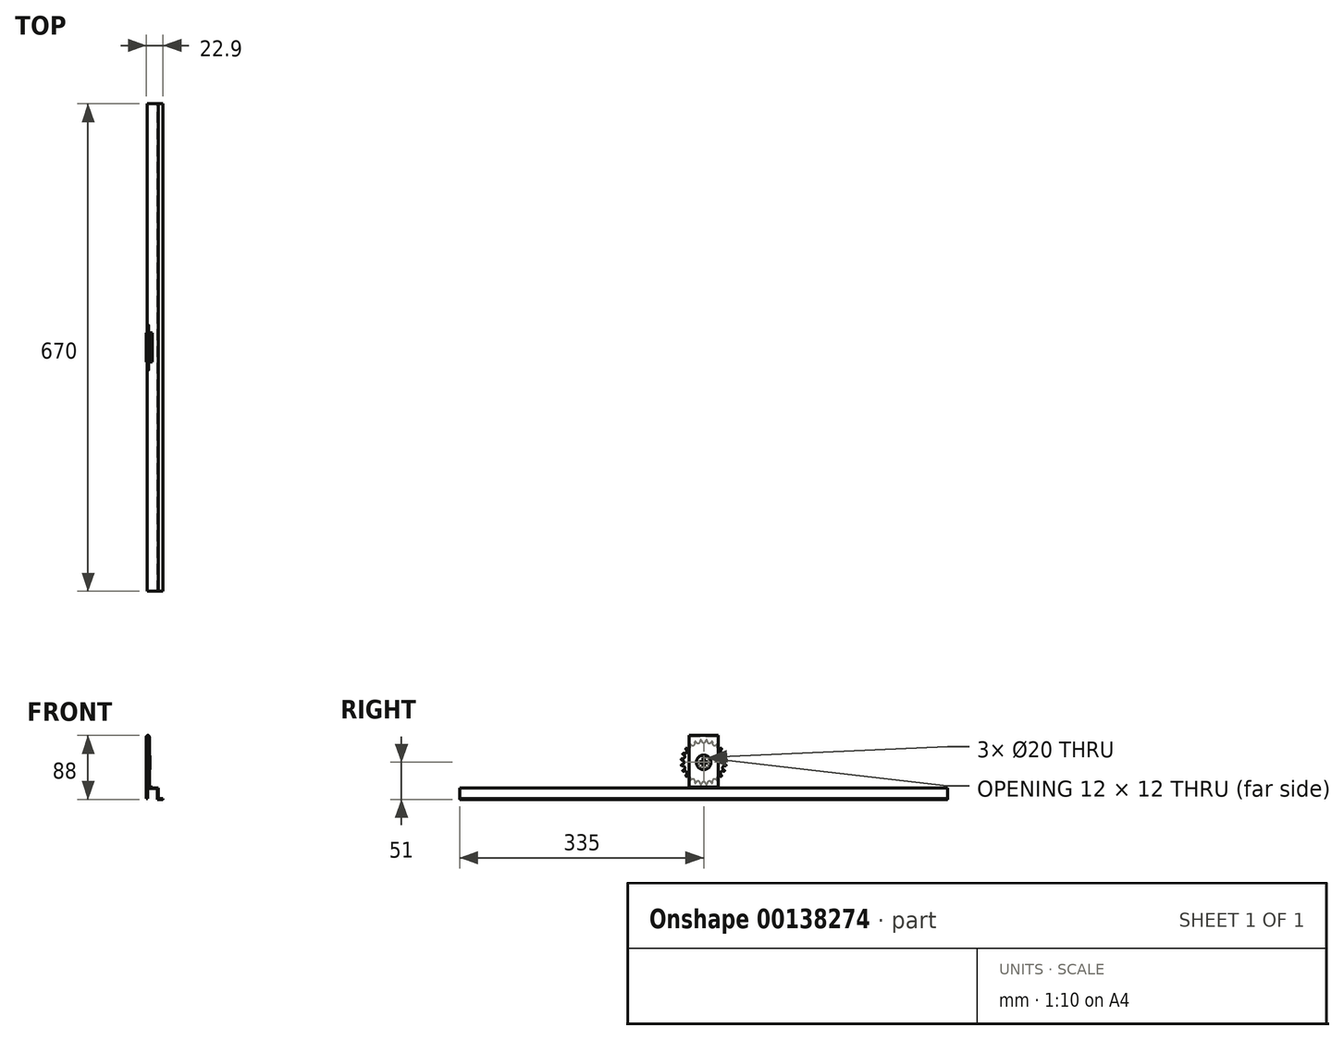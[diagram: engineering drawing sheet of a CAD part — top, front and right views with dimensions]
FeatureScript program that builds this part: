
annotation { "Feature Type Name" : "Feature", "Feature Type Description" : "" }
export const myFeature = defineFeature(function(context is Context, id is Id, definition is map)
    precondition{}
    {
        {
            var Q0;
            Q0=qCreatedBy(makeId("Front.planeOp"),FACE);
            var sketch = newSketch(context, id + "F0", { "sketchPlane" : qUnion([Q0])});
            skLineSegment(sketch, "E0.bottom", {"start": v(0, 0) * mm, "end": v(15, 0) * mm});
            skLineSegment(sketch, "E0.top", {"start": v(1, -1) * mm, "end": v(14, -1) * mm});
            skLineSegment(sketch, "E0.left", {"start": v(0, 0) * mm, "end": v(0, -1) * mm});
            skLineSegment(sketch, "E0.right", {"start": v(15, 0) * mm, "end": v(15, -1) * mm});
            skLineSegment(sketch, "E1.bottom", {"start": v(15, 0) * mm, "end": v(14, 0) * mm});
            skLineSegment(sketch, "E1.top", {"start": v(15, -16) * mm, "end": v(14, -16) * mm});
            skLineSegment(sketch, "E1.left", {"start": v(15, 0) * mm, "end": v(15, -15) * mm});
            skLineSegment(sketch, "E1.right", {"start": v(14, -1) * mm, "end": v(14, -16) * mm});
            skLineSegment(sketch, "E2.bottom", {"start": v(14, -16) * mm, "end": v(21.9, -16) * mm});
            skLineSegment(sketch, "E2.top", {"start": v(15, -15) * mm, "end": v(21.9, -15) * mm});
            skLineSegment(sketch, "E2.left", {"start": v(14, -16) * mm, "end": v(14, -15) * mm});
            skLineSegment(sketch, "E2.right", {"start": v(21.9, -16) * mm, "end": v(21.9, -15) * mm});
            skLineSegment(sketch, "E3.bottom", {"start": v(0, 0) * mm, "end": v(1, 0) * mm});
            skLineSegment(sketch, "E3.top", {"start": v(0, -15) * mm, "end": v(1, -15) * mm});
            skLineSegment(sketch, "E3.left", {"start": v(0, 0) * mm, "end": v(0, -15) * mm});
            skLineSegment(sketch, "E3.right", {"start": v(1, -1) * mm, "end": v(1, -15) * mm});
            skSolve(sketch);
        }
        {
            var Q0;
            Q0=makeQuery(id+"F0.imprint","IMPRINT",FACE,{"disambiguationData":[TD([[makeQuery(id+"F0.imprint","IMPRINT",EDGE,{"derivedFrom":sQuery(id+"F0.wireOp",EDGE,"E0.bottom")}),-1.0]])]});
            extrude(context, id + "F7", {"entities" : qUnion([Q0]), "endBound" : BoundingType.SYMMETRIC, "depth" : 670 * mm});
        }
        {
            var Q0;
            Q0=makeQuery(id+"F7.opExtrude","SWEPT_EDGE",EDGE,{"disambiguationData":[OSD([sQuery(id+"F0.wireOp",EDGE,"E1.bottom"),sQuery(id+"F0.wireOp",EDGE,"E1.left")])]});
            var Q1;
            Q1=makeQuery(id+"F7.opExtrude","SWEPT_EDGE",EDGE,{"disambiguationData":[OSD([sQuery(id+"F0.wireOp",EDGE,"E3.bottom"),sQuery(id+"F0.wireOp",EDGE,"E3.left")])]});
            var Q2;
            Q2=makeQuery(id+"F7.opExtrude","SWEPT_EDGE",EDGE,{"disambiguationData":[OSD([sQuery(id+"F0.wireOp",EDGE,"E1.left"),sQuery(id+"F0.wireOp",EDGE,"E2.top")])]});
            var Q3;
            Q3=makeQuery(id+"F7.opExtrude","SWEPT_EDGE",EDGE,{"disambiguationData":[OSD([sQuery(id+"F0.wireOp",EDGE,"E2.bottom"),sQuery(id+"F0.wireOp",EDGE,"E2.left")])]});
            var Q4;
            Q4=makeQuery(id+"F7.opExtrude","SWEPT_EDGE",EDGE,{"disambiguationData":[OSD([sQuery(id+"F0.wireOp",EDGE,"E0.top"),sQuery(id+"F0.wireOp",EDGE,"E1.right")])]});
            fillet(context, id + "F1", {"entities" : qUnion([Q0, Q1, Q2, Q3, Q4]), "radius" : 1 * mm, "tangentPropagation" : true, "allowEdgeOverflow" : false});
        }
        {
            var Q0;
            Q0=qCreatedBy(makeId("Right.planeOp"),FACE);
            var sketch = newSketch(context, id + "F2", { "sketchPlane" : qUnion([Q0])});
            skLineSegment(sketch, "E4", {"start": v(0, 35) * mm, "end": v(-30, 35) * mm, "construction": true});
            skLineSegment(sketch, "E5", {"start": v(0, 35) * mm, "end": v(-29.74, 38.92) * mm, "construction": true});
            skLineSegment(sketch, "E6", {"start": v(0, 35) * mm, "end": v(-28.98, 42.76) * mm, "construction": true});
            skArc(sketch, "E7", {"start": v(-29.85, 32) * mm, "mid": v(-27, 35) * mm, "end": v(-29.85, 38) * mm});
            skArc(sketch, "E8", {"start": v(-29.6, 39.83) * mm, "mid": v(-29.59, 39.83) * mm, "end": v(-29.56, 39.82) * mm});
            skArc(sketch, "E9", {"start": v(-29.56, 39.82) * mm, "mid": v(-30.66, 39.04) * mm, "end": v(-29.8, 38) * mm});
            skArc(sketch, "E10.trimOffspring", {"start": v(-29.6, 39.83) * mm, "mid": v(-29.6, 39.83) * mm, "end": v(-29.6, 39.83) * mm});
            skArc(sketch, "E11.trimOffspring", {"start": v(-29.85, 38) * mm, "mid": v(-29.85, 38) * mm, "end": v(-29.85, 38) * mm});
            skArc(sketch, "E12.1.0", {"start": v(-29.6, 39.83) * mm, "mid": v(-26.08, 41.99) * mm, "end": v(-28.06, 45.62) * mm});
            skArc(sketch, "E12.1.1", {"start": v(-27.3, 47.3) * mm, "mid": v(-28.57, 46.83) * mm, "end": v(-28.01, 45.6) * mm});
            skArc(sketch, "E12.2.0", {"start": v(-27.35, 47.33) * mm, "mid": v(-23.38, 48.5) * mm, "end": v(-24.35, 52.52) * mm});
            skArc(sketch, "E12.2.1", {"start": v(-23.2, 53.96) * mm, "mid": v(-24.53, 53.83) * mm, "end": v(-24.31, 52.5) * mm});
            skArc(sketch, "E12.3.0", {"start": v(-23.23, 53.99) * mm, "mid": v(-19.1, 54.1) * mm, "end": v(-18.99, 58.23) * mm});
            skArc(sketch, "E12.3.1", {"start": v(-17.5, 59.31) * mm, "mid": v(-18.83, 59.53) * mm, "end": v(-18.96, 58.2) * mm});
            skArc(sketch, "E12.4.0", {"start": v(-17.52, 59.35) * mm, "mid": v(-13.5, 58.38) * mm, "end": v(-12.33, 62.35) * mm});
            skArc(sketch, "E12.4.1", {"start": v(-10.6, 63.01) * mm, "mid": v(-11.83, 63.57) * mm, "end": v(-12.3, 62.3) * mm});
            skArc(sketch, "E12.5.0", {"start": v(-10.62, 63.06) * mm, "mid": v(-6.99, 61.08) * mm, "end": v(-4.83, 64.6) * mm});
            skArc(sketch, "E12.5.1", {"start": v(-3, 64.8) * mm, "mid": v(-4.04, 65.66) * mm, "end": v(-4.82, 64.56) * mm});
            skArc(sketch, "E12.6.0", {"start": v(-3, 64.85) * mm, "mid": v(0, 62) * mm, "end": v(3, 64.85) * mm});
            skArc(sketch, "E12.6.1", {"start": v(4.82, 64.56) * mm, "mid": v(4.04, 65.66) * mm, "end": v(3, 64.8) * mm});
            skArc(sketch, "E12.7.0", {"start": v(4.83, 64.6) * mm, "mid": v(6.99, 61.08) * mm, "end": v(10.62, 63.06) * mm});
            skArc(sketch, "E12.7.1", {"start": v(12.3, 62.3) * mm, "mid": v(11.83, 63.57) * mm, "end": v(10.6, 63.01) * mm});
            skArc(sketch, "E12.8.0", {"start": v(12.33, 62.35) * mm, "mid": v(13.5, 58.38) * mm, "end": v(17.52, 59.35) * mm});
            skArc(sketch, "E12.8.1", {"start": v(18.96, 58.2) * mm, "mid": v(18.83, 59.53) * mm, "end": v(17.5, 59.31) * mm});
            skArc(sketch, "E12.9.0", {"start": v(18.99, 58.23) * mm, "mid": v(19.1, 54.1) * mm, "end": v(23.23, 53.99) * mm});
            skArc(sketch, "E12.9.1", {"start": v(24.31, 52.5) * mm, "mid": v(24.53, 53.83) * mm, "end": v(23.2, 53.96) * mm});
            skArc(sketch, "E12.10.0", {"start": v(24.35, 52.52) * mm, "mid": v(23.38, 48.5) * mm, "end": v(27.35, 47.33) * mm});
            skArc(sketch, "E12.10.1", {"start": v(28.01, 45.6) * mm, "mid": v(28.57, 46.83) * mm, "end": v(27.3, 47.3) * mm});
            skArc(sketch, "E12.11.0", {"start": v(28.06, 45.62) * mm, "mid": v(26.08, 41.99) * mm, "end": v(29.6, 39.83) * mm});
            skArc(sketch, "E12.11.1", {"start": v(29.8, 38) * mm, "mid": v(30.66, 39.04) * mm, "end": v(29.56, 39.82) * mm});
            skArc(sketch, "E12.12.0", {"start": v(29.85, 38) * mm, "mid": v(27, 35) * mm, "end": v(29.85, 32) * mm});
            skArc(sketch, "E12.12.1", {"start": v(29.56, 30.18) * mm, "mid": v(30.66, 30.96) * mm, "end": v(29.8, 32) * mm});
            skArc(sketch, "E12.13.0", {"start": v(29.6, 30.17) * mm, "mid": v(26.08, 28.01) * mm, "end": v(28.06, 24.38) * mm});
            skArc(sketch, "E12.13.1", {"start": v(27.3, 22.7) * mm, "mid": v(28.57, 23.17) * mm, "end": v(28.01, 24.4) * mm});
            skArc(sketch, "E12.14.0", {"start": v(27.35, 22.67) * mm, "mid": v(23.38, 21.5) * mm, "end": v(24.35, 17.48) * mm});
            skArc(sketch, "E12.14.1", {"start": v(23.2, 16.04) * mm, "mid": v(24.53, 16.17) * mm, "end": v(24.31, 17.5) * mm});
            skArc(sketch, "E12.15.0", {"start": v(23.23, 16.01) * mm, "mid": v(19.1, 15.9) * mm, "end": v(18.99, 11.77) * mm});
            skArc(sketch, "E12.15.1", {"start": v(17.5, 10.69) * mm, "mid": v(18.83, 10.47) * mm, "end": v(18.96, 11.8) * mm});
            skArc(sketch, "E12.16.0", {"start": v(17.52, 10.65) * mm, "mid": v(13.5, 11.62) * mm, "end": v(12.33, 7.65) * mm});
            skArc(sketch, "E12.16.1", {"start": v(10.6, 6.99) * mm, "mid": v(11.83, 6.43) * mm, "end": v(12.3, 7.7) * mm});
            skArc(sketch, "E12.17.0", {"start": v(10.62, 6.94) * mm, "mid": v(6.99, 8.92) * mm, "end": v(4.83, 5.4) * mm});
            skArc(sketch, "E12.17.1", {"start": v(3, 5.2) * mm, "mid": v(4.04, 4.34) * mm, "end": v(4.82, 5.44) * mm});
            skArc(sketch, "E12.18.0", {"start": v(3, 5.15) * mm, "mid": v(0, 8) * mm, "end": v(-3, 5.15) * mm});
            skArc(sketch, "E12.18.1", {"start": v(-4.82, 5.44) * mm, "mid": v(-4.04, 4.34) * mm, "end": v(-3, 5.2) * mm});
            skArc(sketch, "E12.19.0", {"start": v(-4.83, 5.4) * mm, "mid": v(-6.99, 8.92) * mm, "end": v(-10.62, 6.94) * mm});
            skArc(sketch, "E12.19.1", {"start": v(-12.3, 7.7) * mm, "mid": v(-11.83, 6.43) * mm, "end": v(-10.6, 6.99) * mm});
            skArc(sketch, "E12.20.0", {"start": v(-12.33, 7.65) * mm, "mid": v(-13.5, 11.62) * mm, "end": v(-17.52, 10.65) * mm});
            skArc(sketch, "E12.20.1", {"start": v(-18.96, 11.8) * mm, "mid": v(-18.83, 10.47) * mm, "end": v(-17.5, 10.69) * mm});
            skArc(sketch, "E12.21.0", {"start": v(-18.99, 11.77) * mm, "mid": v(-19.1, 15.9) * mm, "end": v(-23.23, 16.01) * mm});
            skArc(sketch, "E12.21.1", {"start": v(-24.31, 17.5) * mm, "mid": v(-24.53, 16.17) * mm, "end": v(-23.2, 16.04) * mm});
            skArc(sketch, "E12.22.0", {"start": v(-24.35, 17.48) * mm, "mid": v(-23.38, 21.5) * mm, "end": v(-27.35, 22.67) * mm});
            skArc(sketch, "E12.22.1", {"start": v(-28.01, 24.4) * mm, "mid": v(-28.57, 23.17) * mm, "end": v(-27.3, 22.7) * mm});
            skArc(sketch, "E12.23.0", {"start": v(-28.06, 24.38) * mm, "mid": v(-26.08, 28.01) * mm, "end": v(-29.6, 30.17) * mm});
            skArc(sketch, "E12.23.1", {"start": v(-29.8, 32) * mm, "mid": v(-30.66, 30.96) * mm, "end": v(-29.56, 30.18) * mm});
            skLineSegment(sketch, "E12.anchor2", {"start": v(0, 35) * mm, "end": v(-28.98, 27.24) * mm, "construction": true});
            skLineSegment(sketch, "E13.bottom", {"start": v(1, 41) * mm, "end": v(-1, 41) * mm});
            skLineSegment(sketch, "E13.top", {"start": v(1, 29) * mm, "end": v(-1, 29) * mm});
            skLineSegment(sketch, "E13.left", {"start": v(1, 41) * mm, "end": v(1, 37.3) * mm});
            skLineSegment(sketch, "E13.right", {"start": v(-1, 41) * mm, "end": v(-1, 37.3) * mm});
            skArc(sketch, "E14", {"start": v(-1, 37.3) * mm, "mid": v(-1.77, 36.77) * mm, "end": v(-2.3, 36) * mm});
            skLineSegment(sketch, "E15.bottom", {"start": v(6, 36) * mm, "end": v(2.3, 36) * mm});
            skLineSegment(sketch, "E15.top", {"start": v(6, 34) * mm, "end": v(2.3, 34) * mm});
            skLineSegment(sketch, "E15.left", {"start": v(6, 36) * mm, "end": v(6, 34) * mm});
            skLineSegment(sketch, "E15.right", {"start": v(-6, 36) * mm, "end": v(-6, 34) * mm});
            skLineSegment(sketch, "E16.trimOffspring", {"start": v(-2.3, 36) * mm, "end": v(-6, 36) * mm});
            skLineSegment(sketch, "E17.trimOffspring", {"start": v(1, 32.7) * mm, "end": v(1, 29) * mm});
            skArc(sketch, "E18.trimOffspring", {"start": v(2.3, 36) * mm, "mid": v(1.77, 36.77) * mm, "end": v(1, 37.3) * mm});
            skLineSegment(sketch, "E19.trimOffspring", {"start": v(-2.3, 34) * mm, "end": v(-6, 34) * mm});
            skLineSegment(sketch, "E20.trimOffspring", {"start": v(-1, 32.7) * mm, "end": v(-1, 29) * mm});
            skArc(sketch, "E21.trimOffspring", {"start": v(1, 32.7) * mm, "mid": v(1.77, 33.23) * mm, "end": v(2.3, 34) * mm});
            skArc(sketch, "E22.trimOffspring", {"start": v(-2.3, 34) * mm, "mid": v(-1.77, 33.23) * mm, "end": v(-1, 32.7) * mm});
            skArc(sketch, "E23", {"start": v(-3.7, 44.3) * mm, "mid": v(0, 25) * mm, "end": v(3.7, 44.3) * mm});
            skLineSegment(sketch, "E24", {"start": v(-3.7, 44.3) * mm, "end": v(3.7, 44.3) * mm});
            skSolve(sketch);
        }
        {
            var Q0;
            {var subQ27=sQuery(id+"F2.wireOp",EDGE,"E12.1.1");Q0=makeQuery(id+"F2.imprint","IMPRINT",FACE,{"disambiguationData":[TD([[makeQuery(id+"F2.imprint","IMPRINT",EDGE,{"derivedFrom":subQ27}),1.0]])]});}
            extrude(context, id + "F3", {"entities" : qUnion([Q0]), "depth" : 2 * mm});
        }
        {
            var Q0;
            Q0=makeQuery(id+"F3.opExtrude","CAP_FACE",FACE,{"disambiguationData":[OSD([sQuery(id+"F2.wireOp",EDGE,"E7"),sQuery(id+"F2.wireOp",EDGE,"E9"),sQuery(id+"F2.wireOp",EDGE,"E12.1.0"),sQuery(id+"F2.wireOp",EDGE,"E12.1.1"),sQuery(id+"F2.wireOp",EDGE,"E12.2.0"),sQuery(id+"F2.wireOp",EDGE,"E12.2.1"),sQuery(id+"F2.wireOp",EDGE,"E12.3.0"),sQuery(id+"F2.wireOp",EDGE,"E12.3.1"),sQuery(id+"F2.wireOp",EDGE,"E12.4.0"),sQuery(id+"F2.wireOp",EDGE,"E12.4.1"),sQuery(id+"F2.wireOp",EDGE,"E12.5.0"),sQuery(id+"F2.wireOp",EDGE,"E12.5.1"),sQuery(id+"F2.wireOp",EDGE,"E12.6.0"),sQuery(id+"F2.wireOp",EDGE,"E12.6.1"),sQuery(id+"F2.wireOp",EDGE,"E12.7.0"),sQuery(id+"F2.wireOp",EDGE,"E12.7.1"),sQuery(id+"F2.wireOp",EDGE,"E12.8.0"),sQuery(id+"F2.wireOp",EDGE,"E12.8.1"),sQuery(id+"F2.wireOp",EDGE,"E12.9.0"),sQuery(id+"F2.wireOp",EDGE,"E12.9.1"),sQuery(id+"F2.wireOp",EDGE,"E12.10.0"),sQuery(id+"F2.wireOp",EDGE,"E12.10.1"),sQuery(id+"F2.wireOp",EDGE,"E12.11.0"),sQuery(id+"F2.wireOp",EDGE,"E12.11.1"),sQuery(id+"F2.wireOp",EDGE,"E12.12.0"),sQuery(id+"F2.wireOp",EDGE,"E12.12.1"),sQuery(id+"F2.wireOp",EDGE,"E12.13.0"),sQuery(id+"F2.wireOp",EDGE,"E12.13.1"),sQuery(id+"F2.wireOp",EDGE,"E12.14.0"),sQuery(id+"F2.wireOp",EDGE,"E12.14.1"),sQuery(id+"F2.wireOp",EDGE,"E12.15.0"),sQuery(id+"F2.wireOp",EDGE,"E12.15.1"),sQuery(id+"F2.wireOp",EDGE,"E12.16.0"),sQuery(id+"F2.wireOp",EDGE,"E12.16.1"),sQuery(id+"F2.wireOp",EDGE,"E12.17.0"),sQuery(id+"F2.wireOp",EDGE,"E12.17.1"),sQuery(id+"F2.wireOp",EDGE,"E12.18.0"),sQuery(id+"F2.wireOp",EDGE,"E12.18.1"),sQuery(id+"F2.wireOp",EDGE,"E12.19.0"),sQuery(id+"F2.wireOp",EDGE,"E12.19.1"),sQuery(id+"F2.wireOp",EDGE,"E12.20.0"),sQuery(id+"F2.wireOp",EDGE,"E12.20.1"),sQuery(id+"F2.wireOp",EDGE,"E12.21.0"),sQuery(id+"F2.wireOp",EDGE,"E12.21.1"),sQuery(id+"F2.wireOp",EDGE,"E12.22.0"),sQuery(id+"F2.wireOp",EDGE,"E12.22.1"),sQuery(id+"F2.wireOp",EDGE,"E12.23.0"),sQuery(id+"F2.wireOp",EDGE,"E12.23.1"),sQuery(id+"F2.wireOp",EDGE,"E23"),sQuery(id+"F2.wireOp",EDGE,"E24")])],"isStart":false});
            var sketch = newSketch(context, id + "F8", { "sketchPlane" : qUnion([Q0])});
            skArc(sketch, "E25.0", {"start": v(-3.7, 44.3) * mm, "mid": v(0, 25) * mm, "end": v(3.7, 44.3) * mm});
            skLineSegment(sketch, "E26.0", {"start": v(-3.7, 44.3) * mm, "end": v(3.7, 44.3) * mm});
            skPoint(sketch, "E27.0", {"position": v(1, 41) * mm});
            skPoint(sketch, "E28.1", {"position": v(-1, 29) * mm});
            skPoint(sketch, "E29.0", {"position": v(6, 34) * mm});
            skPoint(sketch, "E30.1", {"position": v(2.3, 36) * mm});
            skArc(sketch, "E31", {"start": v(-1, 37.3) * mm, "mid": v(-1.77, 36.77) * mm, "end": v(-2.3, 36) * mm});
            skLineSegment(sketch, "E32.bottom", {"start": v(1, 41) * mm, "end": v(-1, 41) * mm});
            skLineSegment(sketch, "E32.top", {"start": v(1, 29) * mm, "end": v(-1, 29) * mm});
            skLineSegment(sketch, "E32.left", {"start": v(1, 41) * mm, "end": v(1, 37.3) * mm});
            skLineSegment(sketch, "E32.right", {"start": v(-1, 41) * mm, "end": v(-1, 37.3) * mm});
            skLineSegment(sketch, "E33.bottom", {"start": v(6, 34) * mm, "end": v(2.3, 34) * mm});
            skLineSegment(sketch, "E33.top", {"start": v(6, 36) * mm, "end": v(2.3, 36) * mm});
            skLineSegment(sketch, "E33.left", {"start": v(6, 34) * mm, "end": v(6, 36) * mm});
            skLineSegment(sketch, "E33.right", {"start": v(-6, 34) * mm, "end": v(-6, 36) * mm});
            skLineSegment(sketch, "E34.trimOffspring", {"start": v(-1, 32.7) * mm, "end": v(-1, 29) * mm});
            skLineSegment(sketch, "E35.trimOffspring", {"start": v(-2.3, 36) * mm, "end": v(-6, 36) * mm});
            skArc(sketch, "E36.trimOffspring", {"start": v(-2.3, 34) * mm, "mid": v(-1.77, 33.23) * mm, "end": v(-1, 32.7) * mm});
            skLineSegment(sketch, "E37.trimOffspring", {"start": v(1, 32.7) * mm, "end": v(1, 29) * mm});
            skLineSegment(sketch, "E38.trimOffspring", {"start": v(-2.3, 34) * mm, "end": v(-6, 34) * mm});
            skArc(sketch, "E39.trimOffspring", {"start": v(1, 32.7) * mm, "mid": v(1.77, 33.23) * mm, "end": v(2.3, 34) * mm});
            skArc(sketch, "E40.trimOffspring", {"start": v(2.3, 36) * mm, "mid": v(1.77, 36.77) * mm, "end": v(1, 37.3) * mm});
            skSolve(sketch);
        }
        {
            var Q0;
            Q0=makeQuery(id+"F8.imprint","IMPRINT",FACE,{"disambiguationData":[TD([[makeQuery(id+"F8.imprint","IMPRINT",EDGE,{"derivedFrom":sQuery(id+"F8.wireOp",EDGE,"E25.0")}),1.0]])]});
            extrude(context, id + "F9", {"entities" : qUnion([Q0]), "depth" : 2 * mm, "hasSecondDirection" : true, "secondDirectionOppositeDirection" : true, "secondDirectionDepth" : 4 * mm});
        }
        {
            var Q0;
            Q0=qCreatedBy(makeId("Front.planeOp"),FACE);
            var sketch = newSketch(context, id + "F4", { "sketchPlane" : qUnion([Q0])});
            skLineSegment(sketch, "E41.0", {"start": v(0, 44.3) * mm, "end": v(0, 25) * mm});
            skLineSegment(sketch, "E42.0", {"start": v(2, 44.3) * mm, "end": v(2, 25) * mm});
            skLineSegment(sketch, "E43.0", {"start": v(15, -15) * mm, "end": v(21.9, -15) * mm});
            skLineSegment(sketch, "E44.0", {"start": v(0, 0) * mm, "end": v(15, 0) * mm});
            skLineSegment(sketch, "E45.bottom", {"start": v(0, -15) * mm, "end": v(-1, -15) * mm});
            skLineSegment(sketch, "E45.left", {"start": v(0, -15) * mm, "end": v(0, 70) * mm});
            skLineSegment(sketch, "E45.right", {"start": v(-1, -15) * mm, "end": v(-1, 70) * mm});
            skLineSegment(sketch, "E46.top", {"start": v(2, 0) * mm, "end": v(3, 0) * mm});
            skLineSegment(sketch, "E46.left", {"start": v(2, 70) * mm, "end": v(2, 0) * mm});
            skLineSegment(sketch, "E46.right", {"start": v(3, 70) * mm, "end": v(3, 1) * mm});
            skArc(sketch, "E47", {"start": v(3, 70) * mm, "mid": v(1, 72) * mm, "end": v(-1, 70) * mm});
            skArc(sketch, "E48", {"start": v(2, 70) * mm, "mid": v(1, 71) * mm, "end": v(0, 70) * mm});
            skLineSegment(sketch, "E49.bottom", {"start": v(2, 0) * mm, "end": v(7, 0) * mm});
            skLineSegment(sketch, "E49.top", {"start": v(3, 1) * mm, "end": v(7, 1) * mm});
            skLineSegment(sketch, "E49.left", {"start": v(2, 0) * mm, "end": v(2, 1) * mm});
            skLineSegment(sketch, "E49.right", {"start": v(7, 0) * mm, "end": v(7, 1) * mm});
            skSolve(sketch);
        }
        {
            var Q0;
            {var subQ0=sQuery(id+"F4.wireOp",EDGE,"E45.bottom");Q0=makeQuery(id+"F4.imprint","IMPRINT",FACE,{"disambiguationData":[TD([[makeQuery(id+"F4.imprint","IMPRINT",EDGE,{"derivedFrom":subQ0}),-1.0]])]});}
            extrude(context, id + "F10", {"entities" : qUnion([Q0]), "endBound" : BoundingType.SYMMETRIC, "depth" : 40 * mm});
        }
        {
            var Q0;
            Q0=makeQuery(id+"F10.opExtrude","SWEPT_FACE",FACE,{"disambiguationData":[OSD([sQuery(id+"F4.wireOp",EDGE,"E46.right")])]});
            var sketch = newSketch(context, id + "F5", { "sketchPlane" : qUnion([Q0])});
            skArc(sketch, "E50.0", {"start": v(-3.7, 44.3) * mm, "mid": v(0, 25) * mm, "end": v(3.7, 44.3) * mm});
            skCircle(sketch, "E51", {"center": v(0, 35) * mm, "radius": 10 * mm});
            skSolve(sketch);
        }
        {
            var Q0;
            Q0=makeQuery(id+"F5.imprint","IMPRINT",FACE,{"disambiguationData":[TD([[makeQuery(id+"F5.imprint","IMPRINT",EDGE,{"derivedFrom":sQuery(id+"F5.wireOp",EDGE,"E50.0")}),1.0]])]});
            var Q1;
            {var subQ0=sQuery(id+"F5.wireOp",EDGE,"E51");var subQ1=makeQuery(id+"F5.imprint","IMPRINT",VERTEX,{"disambiguationData":[OD(0.0)],"derivedFrom":subQ0});Q1=makeQuery(id+"F5.imprint","IMPRINT",FACE,{"disambiguationData":[TD([[makeQuery(id+"F5.imprint","IMPRINT",EDGE,{"disambiguationData":[TD([[subQ1,1.0]])],"derivedFrom":subQ0}),1.0]])]});}
            var Q2;
            Q2=sQuery(id+"F5.wireOp",EDGE,"E50.0");
            var Q3;
            Q3=sQuery(id+"F5.wireOp",EDGE,"68b923b3-dc10-40f2-90da-8eb72fc5caed.0");
            extrude(context, id + "F11", {"entities" : qUnion([Q0, Q1]), "operationType" : NewBodyOperationType.REMOVE, "surfaceEntities" : qUnion([Q2, Q3]), "oppositeDirection" : true, "depth" : 25 * mm});
        }
        {
            var Q0;
            Q0=makeQuery(id+"F10.opExtrude","SWEPT_EDGE",EDGE,{"disambiguationData":[OSD([sQuery(id+"F4.wireOp",EDGE,"E46.right"),sQuery(id+"F4.wireOp",EDGE,"E49.top")])]});
            var Q1;
            Q1=makeQuery(id+"F10.opExtrude","SWEPT_EDGE",EDGE,{"disambiguationData":[OSD([sQuery(id+"F4.wireOp",EDGE,"E44.0"),sQuery(id+"F4.wireOp",EDGE,"E49.bottom"),sQuery(id+"F4.wireOp",EDGE,"E49.left")])]});
            fillet(context, id + "F6", {"entities" : qUnion([Q0, Q1]), "radius" : 1 * mm, "tangentPropagation" : true, "allowEdgeOverflow" : false});
        }
    });
